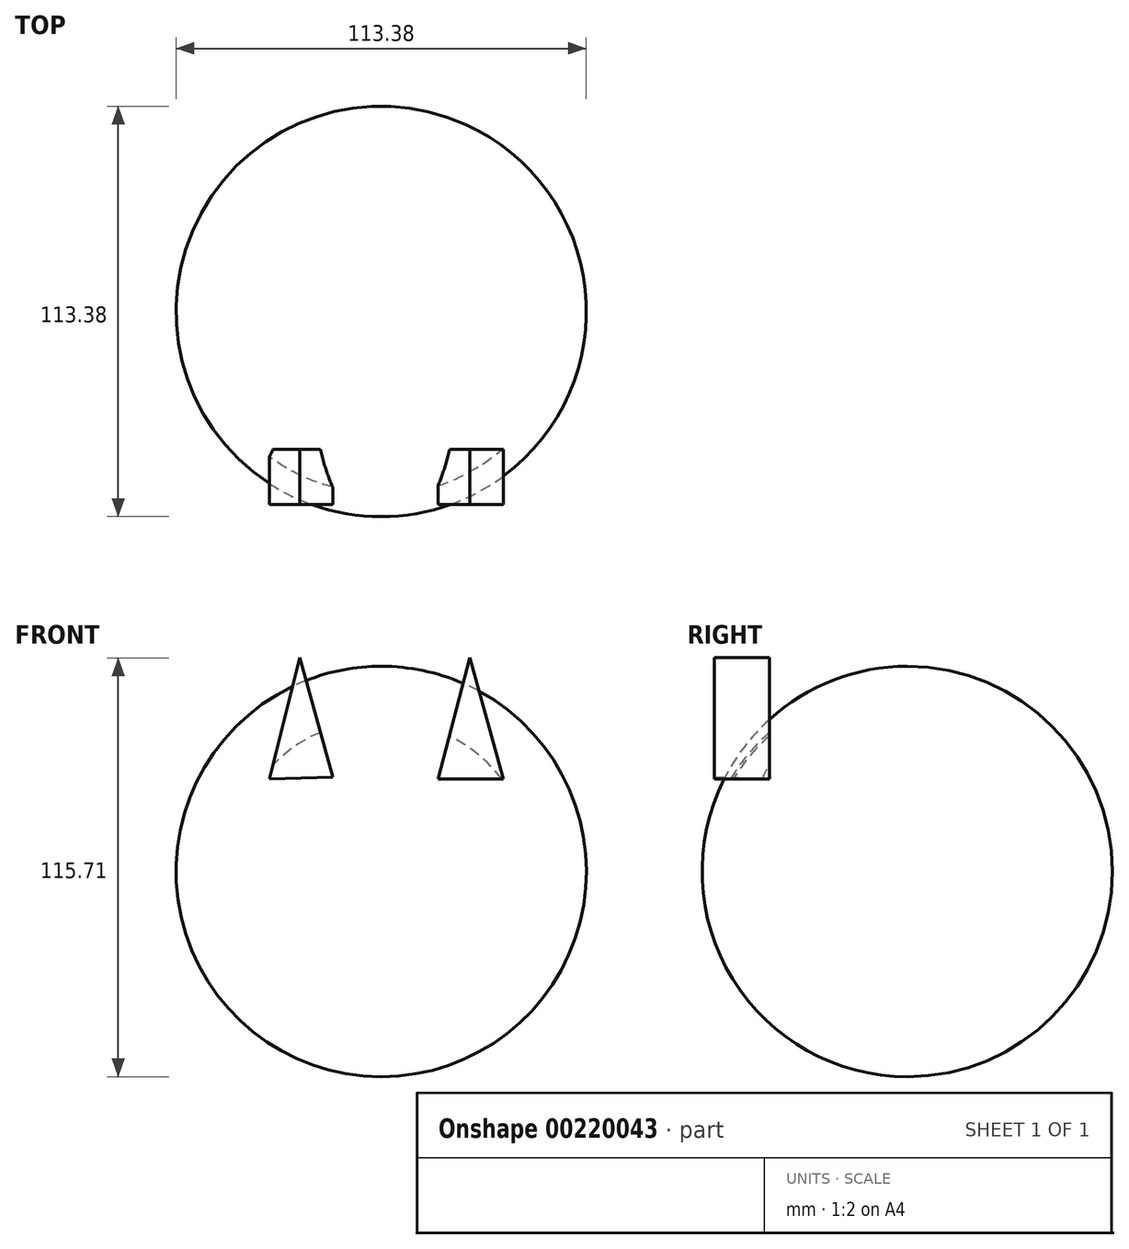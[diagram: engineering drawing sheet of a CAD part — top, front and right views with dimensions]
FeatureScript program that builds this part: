
annotation { "Feature Type Name" : "Feature", "Feature Type Description" : "" }
export const myFeature = defineFeature(function(context is Context, id is Id, definition is map)
    precondition{}
    {
        {
            var Q0;
            Q0=qCreatedBy(makeId("Front.planeOp"),FACE);
            var sketch = newSketch(context, id + "F0", { "sketchPlane" : qUnion([Q0])});
            skArc(sketch, "E0", {"start": v(0, -56.7) * mm, "mid": v(56.7, 0) * mm, "end": v(0, 56.7) * mm});
            skLineSegment(sketch, "E1", {"start": v(0, 69.8) * mm, "end": v(0, -68.35) * mm});
            skSolve(sketch);
        }
        {
            var Q0;
            {var subQ0=sQuery(id+"F0.wireOp",EDGE,"E0");Q0=makeQuery(id+"F0.imprint","IMPRINT",FACE,{"disambiguationData":[TD([[makeQuery(id+"F0.imprint","IMPRINT",EDGE,{"derivedFrom":subQ0}),1.0]])]});}
            var Q1;
            Q1=sQuery(id+"F0.wireOp",EDGE,"E1");
            revolve(context, id + "F1", {"entities" : qUnion([Q0]), "axis" : qUnion([Q1]), "revolveType" : RevolveType.FULL});
        }
        {
            var Q0;
            Q0=qCreatedBy(makeId("Front.planeOp"),FACE);
            cPlane(context, id + "F2", {"entities" : qUnion([Q0]), "cplaneType" : CPlaneType.OFFSET, "offset" : 38.1 * mm, "width" : 152.4 * mm, "height" : 152.4 * mm});
        }
        {
            var Q0;
            Q0=qCreatedBy(id+"F2.planeOp",FACE);
            var sketch = newSketch(context, id + "F3", { "sketchPlane" : qUnion([Q0])});
            skLineSegment(sketch, "E2", {"start": v(-30.9, 25.5) * mm, "end": v(-22.44, 59.02) * mm});
            skLineSegment(sketch, "E3", {"start": v(-22.44, 59.02) * mm, "end": v(-13.4, 26.09) * mm});
            skLineSegment(sketch, "E4", {"start": v(-13.4, 26.09) * mm, "end": v(-30.9, 25.5) * mm});
            skLineSegment(sketch, "E5", {"start": v(15.74, 25.5) * mm, "end": v(33.81, 25.5) * mm});
            skLineSegment(sketch, "E6", {"start": v(33.81, 25.5) * mm, "end": v(24.48, 59.02) * mm});
            skLineSegment(sketch, "E7", {"start": v(24.48, 59.02) * mm, "end": v(15.74, 25.5) * mm});
            skSolve(sketch);
        }
        {
            var Q0;
            Q0 = qSketchRegion(id + "F3", true);
            extrude(context, id + "F4", {"entities" : qUnion([Q0]), "operationType" : NewBodyOperationType.ADD, "depth" : 15.24 * mm});
        }
    });
